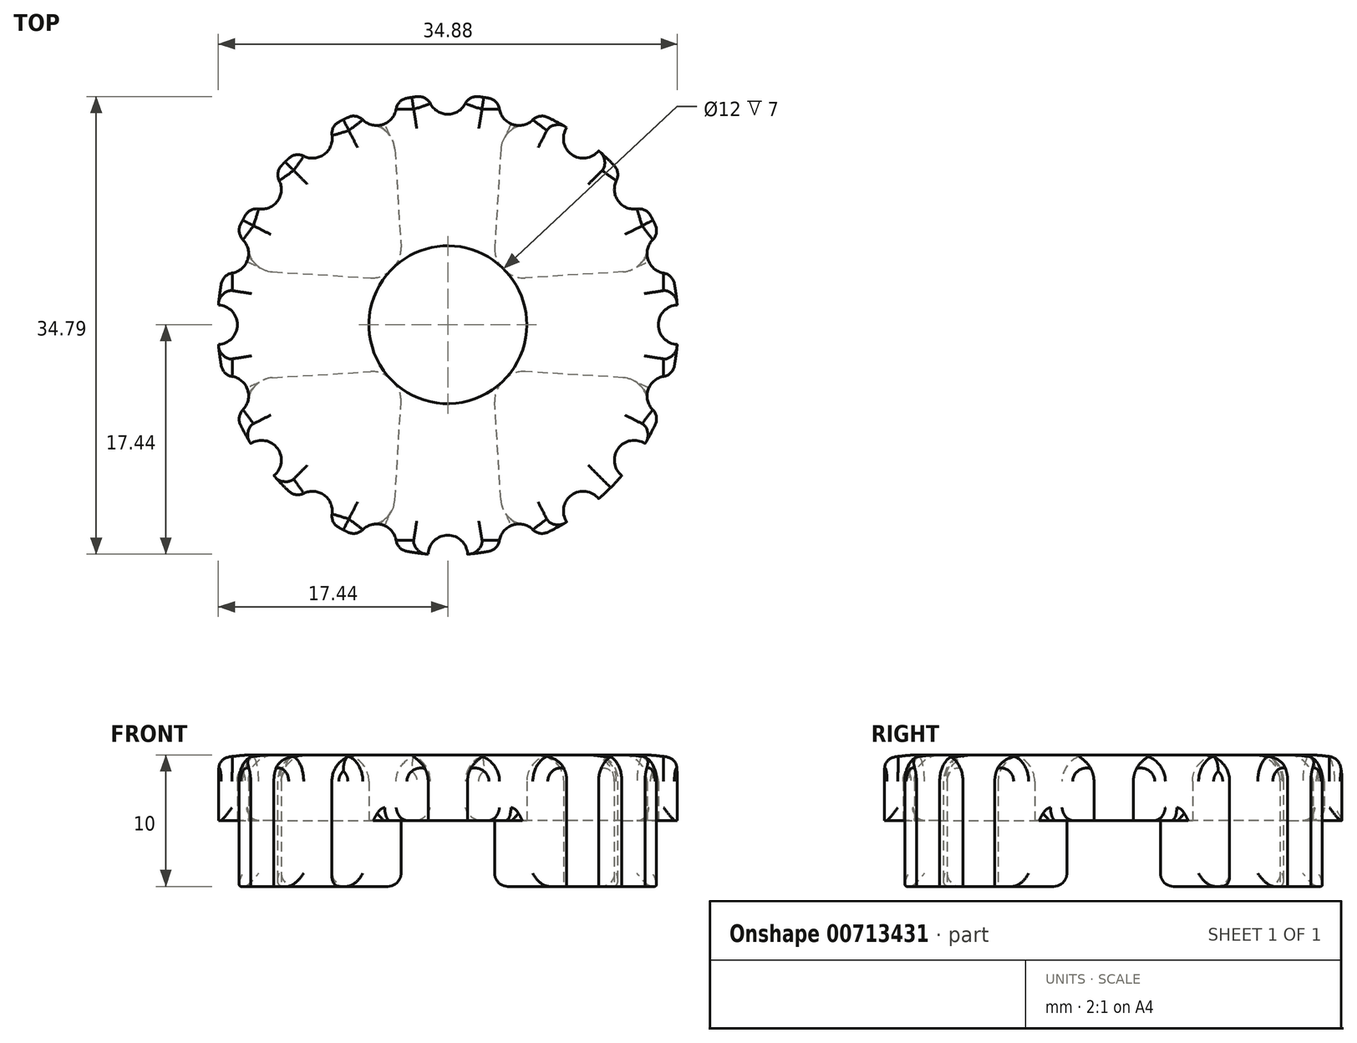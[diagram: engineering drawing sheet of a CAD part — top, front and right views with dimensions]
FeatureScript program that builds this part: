
annotation { "Feature Type Name" : "Feature", "Feature Type Description" : "" }
export const myFeature = defineFeature(function(context is Context, id is Id, definition is map)
    precondition{}
    {
        {
            var Q0;
            Q0=qCreatedBy(makeId("Top.planeOp"),FACE);
            var sketch = newSketch(context, id + "F0", { "sketchPlane" : qUnion([Q0])});
            skCircle(sketch, "E0", {"center": v(0, 0) * mm, "radius": 17.5 * mm});
            skCircle(sketch, "E1", {"center": v(0, 0) * mm, "radius": 6 * mm});
            skPoint(sketch, "E2", {"position": v(-3.5, 4.87) * mm});
            skPoint(sketch, "E3.MirrorP", {"position": v(3.5, 4.87) * mm});
            skPoint(sketch, "E4", {"position": v(-4.25, 16.98) * mm});
            skPoint(sketch, "E5.MirrorP", {"position": v(4.25, 16.98) * mm});
            skLineSegment(sketch, "E6", {"start": v(-4.25, 16.98) * mm, "end": v(-3.5, 4.87) * mm});
            skLineSegment(sketch, "E7", {"start": v(4.25, 16.98) * mm, "end": v(3.5, 4.87) * mm});
            skLineSegment(sketch, "E8.1.0", {"start": v(-16.98, 4.25) * mm, "end": v(-4.87, 3.5) * mm});
            skLineSegment(sketch, "E8.1.1", {"start": v(-16.98, -4.25) * mm, "end": v(-4.87, -3.5) * mm});
            skLineSegment(sketch, "E8.2.0", {"start": v(-4.25, -16.98) * mm, "end": v(-3.5, -4.87) * mm});
            skLineSegment(sketch, "E8.2.1", {"start": v(4.25, -16.98) * mm, "end": v(3.5, -4.87) * mm});
            skLineSegment(sketch, "E8.3.0", {"start": v(16.98, -4.25) * mm, "end": v(4.87, -3.5) * mm});
            skLineSegment(sketch, "E8.3.1", {"start": v(16.98, 4.25) * mm, "end": v(4.87, 3.5) * mm});
            skCircle(sketch, "E9", {"center": v(0, 17.5) * mm, "radius": 1.5 * mm});
            skCircle(sketch, "E10.1.0", {"center": v(-5.4, 16.64) * mm, "radius": 1.5 * mm});
            skCircle(sketch, "E10.2.0", {"center": v(-10.29, 14.16) * mm, "radius": 1.5 * mm});
            skCircle(sketch, "E11.1.3.0", {"center": v(-14.16, 10.29) * mm, "radius": 1.5 * mm});
            skCircle(sketch, "E11.1.4.0", {"center": v(-16.64, 5.4) * mm, "radius": 1.5 * mm});
            skCircle(sketch, "E11.1.5.0", {"center": v(-17.5, 0) * mm, "radius": 1.5 * mm});
            skCircle(sketch, "E11.1.6.0", {"center": v(-16.64, -5.4) * mm, "radius": 1.5 * mm});
            skCircle(sketch, "E11.1.7.0", {"center": v(-14.16, -10.29) * mm, "radius": 1.5 * mm});
            skCircle(sketch, "E11.1.8.0", {"center": v(-10.29, -14.16) * mm, "radius": 1.5 * mm});
            skCircle(sketch, "E11.1.9.0", {"center": v(-5.4, -16.64) * mm, "radius": 1.5 * mm});
            skCircle(sketch, "E11.1.10.0", {"center": v(0, -17.5) * mm, "radius": 1.5 * mm});
            skCircle(sketch, "E11.1.11.0", {"center": v(5.4, -16.64) * mm, "radius": 1.5 * mm});
            skCircle(sketch, "E11.1.12.0", {"center": v(10.29, -14.16) * mm, "radius": 1.5 * mm});
            skCircle(sketch, "E11.1.13.0", {"center": v(14.16, -10.29) * mm, "radius": 1.5 * mm});
            skCircle(sketch, "E11.1.14.0", {"center": v(16.64, -5.4) * mm, "radius": 1.5 * mm});
            skCircle(sketch, "E11.1.15.0", {"center": v(17.5, 0) * mm, "radius": 1.5 * mm});
            skCircle(sketch, "E11.1.16.0", {"center": v(16.64, 5.4) * mm, "radius": 1.5 * mm});
            skCircle(sketch, "E11.1.17.0", {"center": v(14.16, 10.29) * mm, "radius": 1.5 * mm});
            skCircle(sketch, "E11.1.18.0", {"center": v(10.29, 14.16) * mm, "radius": 1.5 * mm});
            skCircle(sketch, "E11.1.19.0", {"center": v(5.4, 16.64) * mm, "radius": 1.5 * mm});
            skSolve(sketch);
        }
        {
            var Q0;
            {var subQ0=sQuery(id+"F0.wireOp",EDGE,"E11.1.6.0");var subQ6=sQuery(id+"F0.wireOp",EDGE,"E0");var subQ14=makeQuery(id+"F0.imprint","INTERSECT",VERTEX,{"disambiguationData":[OD(1.0)],"derivedFrom":[subQ6,subQ0]});Q0=makeQuery(id+"F0.imprint","IMPRINT",FACE,{"disambiguationData":[TD([[makeQuery(id+"F0.imprint","IMPRINT",EDGE,{"disambiguationData":[TD([[subQ14,-1.0]])],"derivedFrom":subQ6}),1.0]])]});}
            var Q1;
            {var subQ0=sQuery(id+"F0.wireOp",EDGE,"E11.1.11.0");var subQ5=sQuery(id+"F0.wireOp",EDGE,"E0");var subQ6=makeQuery(id+"F0.imprint","INTERSECT",VERTEX,{"disambiguationData":[OD(1.0)],"derivedFrom":[subQ5,subQ0]});Q1=makeQuery(id+"F0.imprint","IMPRINT",FACE,{"disambiguationData":[TD([[makeQuery(id+"F0.imprint","IMPRINT",EDGE,{"disambiguationData":[TD([[subQ6,-1.0]])],"derivedFrom":subQ5}),1.0]])]});}
            var Q2;
            {var subQ1=sQuery(id+"F0.wireOp",EDGE,"E0");var subQ12=sQuery(id+"F0.wireOp",EDGE,"E11.1.16.0");var subQ13=makeQuery(id+"F0.imprint","INTERSECT",VERTEX,{"disambiguationData":[OD(1.0)],"derivedFrom":[subQ1,subQ12]});Q2=makeQuery(id+"F0.imprint","IMPRINT",FACE,{"disambiguationData":[TD([[makeQuery(id+"F0.imprint","IMPRINT",EDGE,{"disambiguationData":[TD([[subQ13,-1.0]])],"derivedFrom":subQ1}),1.0]])]});}
            var Q3;
            {var subQ1=sQuery(id+"F0.wireOp",EDGE,"E0");var subQ12=sQuery(id+"F0.wireOp",EDGE,"E10.1.0");var subQ15=makeQuery(id+"F0.imprint","INTERSECT",VERTEX,{"disambiguationData":[OD(1.0)],"derivedFrom":[subQ1,subQ12]});Q3=makeQuery(id+"F0.imprint","IMPRINT",FACE,{"disambiguationData":[TD([[makeQuery(id+"F0.imprint","IMPRINT",EDGE,{"disambiguationData":[TD([[subQ15,-1.0]])],"derivedFrom":subQ1}),1.0]])]});}
            extrude(context, id + "F1", {"entities" : qUnion([Q0, Q1, Q2, Q3]), "depth" : 10 * mm, "offsetDistance" : 25 * mm});
        }
        {
            var Q0;
            {var subQ5=sQuery(id+"F0.wireOp",EDGE,"E11.1.9.0");var subQ6=sQuery(id+"F0.wireOp",EDGE,"E0");var subQ7=makeQuery(id+"F0.imprint","INTERSECT",VERTEX,{"disambiguationData":[OD(1.0)],"derivedFrom":[subQ6,subQ5]});Q0=makeQuery(id+"F0.imprint","IMPRINT",FACE,{"disambiguationData":[TD([[makeQuery(id+"F0.imprint","IMPRINT",EDGE,{"disambiguationData":[TD([[subQ7,-1.0]])],"derivedFrom":subQ6}),1.0]])]});}
            var Q1;
            {var subQ8=sQuery(id+"F0.wireOp",EDGE,"E0");var subQ14=sQuery(id+"F0.wireOp",EDGE,"E11.1.4.0");var subQ15=makeQuery(id+"F0.imprint","INTERSECT",VERTEX,{"disambiguationData":[OD(1.0)],"derivedFrom":[subQ8,subQ14]});Q1=makeQuery(id+"F0.imprint","IMPRINT",FACE,{"disambiguationData":[TD([[makeQuery(id+"F0.imprint","IMPRINT",EDGE,{"disambiguationData":[TD([[subQ15,-1.0]])],"derivedFrom":subQ8}),1.0]])]});}
            var Q2;
            {var subQ6=sQuery(id+"F0.wireOp",EDGE,"E0");var subQ13=sQuery(id+"F0.wireOp",EDGE,"E11.1.16.0");var subQ14=makeQuery(id+"F0.imprint","INTERSECT",VERTEX,{"disambiguationData":[OD(0.0)],"derivedFrom":[subQ6,subQ13]});Q2=makeQuery(id+"F0.imprint","IMPRINT",FACE,{"disambiguationData":[TD([[makeQuery(id+"F0.imprint","IMPRINT",EDGE,{"disambiguationData":[TD([[subQ14,1.0]])],"derivedFrom":subQ6}),1.0]])]});}
            var Q3;
            {var subQ5=sQuery(id+"F0.wireOp",EDGE,"E11.1.19.0");var subQ14=sQuery(id+"F0.wireOp",EDGE,"E0");var subQ17=makeQuery(id+"F0.imprint","INTERSECT",VERTEX,{"disambiguationData":[OD(1.0)],"derivedFrom":[subQ14,subQ5]});Q3=makeQuery(id+"F0.imprint","IMPRINT",FACE,{"disambiguationData":[TD([[makeQuery(id+"F0.imprint","IMPRINT",EDGE,{"disambiguationData":[TD([[subQ17,-1.0]])],"derivedFrom":subQ14}),1.0]])]});}
            var Q4;
            {var subQ0=sQuery(id+"F0.wireOp",EDGE,"E6");var subQ1=sQuery(id+"F0.wireOp",EDGE,"E1");var subQ2=makeQuery(id+"F0.imprint","INTERSECT",VERTEX,{"derivedFrom":[subQ1,subQ0]});Q4=makeQuery(id+"F0.imprint","IMPRINT",FACE,{"disambiguationData":[TD([[makeQuery(id+"F0.imprint","IMPRINT",EDGE,{"disambiguationData":[TD([[subQ2,1.0]])],"derivedFrom":subQ1}),-1.0]])]});}
            var Q5;
            {var subQ0=sQuery(id+"F0.wireOp",EDGE,"E7");var subQ1=sQuery(id+"F0.wireOp",EDGE,"E1");var subQ2=makeQuery(id+"F0.imprint","INTERSECT",VERTEX,{"derivedFrom":[subQ1,subQ0]});Q5=makeQuery(id+"F0.imprint","IMPRINT",FACE,{"disambiguationData":[TD([[makeQuery(id+"F0.imprint","IMPRINT",EDGE,{"disambiguationData":[TD([[subQ2,-1.0]])],"derivedFrom":subQ1}),-1.0]])]});}
            var Q6;
            {var subQ0=sQuery(id+"F0.wireOp",EDGE,"E8.2.1");var subQ1=sQuery(id+"F0.wireOp",EDGE,"E1");var subQ2=makeQuery(id+"F0.imprint","INTERSECT",VERTEX,{"derivedFrom":[subQ1,subQ0]});Q6=makeQuery(id+"F0.imprint","IMPRINT",FACE,{"disambiguationData":[TD([[makeQuery(id+"F0.imprint","IMPRINT",EDGE,{"disambiguationData":[TD([[subQ2,1.0]])],"derivedFrom":subQ1}),-1.0]])]});}
            var Q7;
            {var subQ0=sQuery(id+"F0.wireOp",EDGE,"E8.1.1");var subQ1=sQuery(id+"F0.wireOp",EDGE,"E1");var subQ2=makeQuery(id+"F0.imprint","INTERSECT",VERTEX,{"derivedFrom":[subQ1,subQ0]});Q7=makeQuery(id+"F0.imprint","IMPRINT",FACE,{"disambiguationData":[TD([[makeQuery(id+"F0.imprint","IMPRINT",EDGE,{"disambiguationData":[TD([[subQ2,1.0]])],"derivedFrom":subQ1}),-1.0]])]});}
            extrude(context, id + "F2", {"entities" : qUnion([Q0, Q1, Q2, Q3, Q4, Q5, Q6, Q7]), "operationType" : NewBodyOperationType.ADD, "depth" : 10 * mm, "offsetDistance" : 25 * mm, "hasSecondDirection" : true, "secondDirectionOppositeDirection" : false, "secondDirectionDepth" : 5 * mm});
        }
        {
            var Q0;
            {var subQ0=sQuery(id+"F0.wireOp",EDGE,"E11.1.24.0");var subQ1=sQuery(id+"F0.wireOp",EDGE,"E11.1.20.0");var subQ2=sQuery(id+"F0.wireOp",EDGE,"E11.1.14.0");var subQ3=sQuery(id+"F0.wireOp",EDGE,"E11.1.11.0");var subQ4=sQuery(id+"F0.wireOp",EDGE,"E11.1.5.0");var subQ5=sQuery(id+"F0.wireOp",EDGE,"E10.1.0");var subQ6=sQuery(id+"F0.wireOp",EDGE,"E8.3.1");var subQ7=sQuery(id+"F0.wireOp",EDGE,"E8.3.0");var subQ8=sQuery(id+"F0.wireOp",EDGE,"E8.2.1");var subQ9=sQuery(id+"F0.wireOp",EDGE,"E8.2.0");var subQ10=sQuery(id+"F0.wireOp",EDGE,"E8.1.1");var subQ11=sQuery(id+"F0.wireOp",EDGE,"E8.1.0");var subQ12=sQuery(id+"F0.wireOp",EDGE,"E7");var subQ13=sQuery(id+"F0.wireOp",EDGE,"E6");var subQ14=sQuery(id+"F0.wireOp",EDGE,"E0");Q0=makeQuery(id+"F2.boolean.opBoolean","MERGE",FACE,{"derivedFrom":[makeQuery(id+"F1.opExtrude","CAP_FACE",FACE,{"disambiguationData":[OSD([subQ14,subQ12,subQ6,subQ1,sQuery(id+"F0.wireOp",EDGE,"E11.1.21.0"),sQuery(id+"F0.wireOp",EDGE,"E11.1.22.0"),sQuery(id+"F0.wireOp",EDGE,"E11.1.23.0"),subQ0])],"isStart":false}),makeQuery(id+"F1.opExtrude","CAP_FACE",FACE,{"disambiguationData":[OSD([subQ14,subQ13,subQ11,subQ5,sQuery(id+"F0.wireOp",EDGE,"E10.2.0"),sQuery(id+"F0.wireOp",EDGE,"E11.1.3.0"),sQuery(id+"F0.wireOp",EDGE,"E11.1.4.0"),subQ4])],"isStart":false}),makeQuery(id+"F1.opExtrude","CAP_FACE",FACE,{"disambiguationData":[OSD([subQ14,subQ10,subQ9,sQuery(id+"F0.wireOp",EDGE,"E11.1.8.0"),sQuery(id+"F0.wireOp",EDGE,"E11.1.9.0"),sQuery(id+"F0.wireOp",EDGE,"E11.1.10.0"),subQ3])],"isStart":false}),makeQuery(id+"F1.opExtrude","CAP_FACE",FACE,{"disambiguationData":[OSD([subQ14,subQ8,subQ7,subQ2,sQuery(id+"F0.wireOp",EDGE,"E11.1.15.0"),sQuery(id+"F0.wireOp",EDGE,"E11.1.16.0"),sQuery(id+"F0.wireOp",EDGE,"E11.1.17.0")])],"isStart":false}),makeQuery(id+"F2.opExtrude","CAP_FACE",FACE,{"disambiguationData":[OSD([subQ14,sQuery(id+"F0.wireOp",EDGE,"E1"),subQ13,subQ12,subQ11,subQ10,subQ9,subQ8,subQ7,subQ6,sQuery(id+"F0.wireOp",EDGE,"E9"),subQ5,subQ4,sQuery(id+"F0.wireOp",EDGE,"E11.1.6.0"),sQuery(id+"F0.wireOp",EDGE,"E11.1.7.0"),subQ3,sQuery(id+"F0.wireOp",EDGE,"E11.1.12.0"),sQuery(id+"F0.wireOp",EDGE,"E11.1.13.0"),subQ2,sQuery(id+"F0.wireOp",EDGE,"E11.1.18.0"),sQuery(id+"F0.wireOp",EDGE,"E11.1.19.0"),subQ1,subQ0])],"isStart":false})]});}
            var Q1;
            Q1=makeQuery(id+"F1.opExtrude","SWEPT_EDGE",EDGE,{"disambiguationData":[OSD([sQuery(id+"F0.wireOp",EDGE,"E6"),sQuery(id+"F0.wireOp",EDGE,"E8.1.0")])]});
            var Q2;
            Q2=makeQuery(id+"F1.opExtrude","SWEPT_EDGE",EDGE,{"disambiguationData":[OSD([sQuery(id+"F0.wireOp",EDGE,"E8.1.1"),sQuery(id+"F0.wireOp",EDGE,"E8.2.0")])]});
            var Q3;
            Q3=makeQuery(id+"F1.opExtrude","SWEPT_EDGE",EDGE,{"disambiguationData":[OSD([sQuery(id+"F0.wireOp",EDGE,"E8.2.1"),sQuery(id+"F0.wireOp",EDGE,"E8.3.0")])]});
            var Q4;
            Q4=makeQuery(id+"F1.opExtrude","SWEPT_EDGE",EDGE,{"disambiguationData":[OSD([sQuery(id+"F0.wireOp",EDGE,"E7"),sQuery(id+"F0.wireOp",EDGE,"E8.3.1")])]});
            fillet(context, id + "F3", {"entities" : qUnion([Q0, Q1, Q2, Q3, Q4]), "radius" : 2 * mm, "tangentPropagation" : true, "allowEdgeOverflow" : false});
        }
        {
            var Q0;
            Q0=makeQuery(id+"F1.opExtrude","SWEPT_FACE",FACE,{"disambiguationData":[OSD([sQuery(id+"F0.wireOp",EDGE,"E11.1.8.0")])]});
            var Q1;
            Q1=makeQuery(id+"F1.opExtrude","SWEPT_FACE",FACE,{"disambiguationData":[OSD([sQuery(id+"F0.wireOp",EDGE,"E11.1.9.0")])]});
            var Q2;
            Q2=makeQuery(id+"F1.opExtrude","SWEPT_FACE",FACE,{"disambiguationData":[OSD([sQuery(id+"F0.wireOp",EDGE,"E11.1.10.0")])]});
            var Q3;
            {var subQ0=sQuery(id+"F0.wireOp",EDGE,"E11.1.11.0");Q3=makeQuery(id+"F3.opFillet","BLEND_EDGE",EDGE,{"blendedFrom":[makeQuery(id+"F1.opExtrude","CAP_EDGE",EDGE,{"disambiguationData":[OSD([sQuery(id+"F0.wireOp",EDGE,"E11.1.10.0")])],"isStart":false}),makeQuery(id+"F2.boolean.opBoolean","MERGE",EDGE,{"derivedFrom":[makeQuery(id+"F1.opExtrude","CAP_EDGE",EDGE,{"disambiguationData":[OSD([subQ0])],"isStart":false}),makeQuery(id+"F2.opExtrude","CAP_EDGE",EDGE,{"disambiguationData":[OSD([subQ0])],"isStart":false})]})],"blendedInto":[]});}
            var Q4;
            {var subQ0=sQuery(id+"F0.wireOp",EDGE,"E11.1.11.0");Q4=makeQuery(id+"F2.boolean.opBoolean","MERGE",FACE,{"derivedFrom":[makeQuery(id+"F1.opExtrude","SWEPT_FACE",FACE,{"disambiguationData":[OSD([subQ0])]}),makeQuery(id+"F2.opExtrude","SWEPT_FACE",FACE,{"disambiguationData":[OSD([subQ0])]})]});}
            var Q5;
            Q5=makeQuery(id+"F2.opExtrude","SWEPT_FACE",FACE,{"disambiguationData":[OSD([sQuery(id+"F0.wireOp",EDGE,"E11.1.12.0")])]});
            var Q6;
            Q6=makeQuery(id+"F2.opExtrude","SWEPT_FACE",FACE,{"disambiguationData":[OSD([sQuery(id+"F0.wireOp",EDGE,"E11.1.13.0")])]});
            var Q7;
            {var subQ0=sQuery(id+"F0.wireOp",EDGE,"E11.1.14.0");Q7=makeQuery(id+"F2.boolean.opBoolean","MERGE",FACE,{"derivedFrom":[makeQuery(id+"F1.opExtrude","SWEPT_FACE",FACE,{"disambiguationData":[OSD([subQ0])]}),makeQuery(id+"F2.opExtrude","SWEPT_FACE",FACE,{"disambiguationData":[OSD([subQ0])]})]});}
            var Q8;
            Q8=makeQuery(id+"F1.opExtrude","SWEPT_FACE",FACE,{"disambiguationData":[OSD([sQuery(id+"F0.wireOp",EDGE,"E11.1.15.0")])]});
            var Q9;
            Q9=makeQuery(id+"F1.opExtrude","SWEPT_FACE",FACE,{"disambiguationData":[OSD([sQuery(id+"F0.wireOp",EDGE,"E11.1.16.0")])]});
            var Q10;
            Q10=makeQuery(id+"F1.opExtrude","SWEPT_FACE",FACE,{"disambiguationData":[OSD([sQuery(id+"F0.wireOp",EDGE,"E11.1.17.0")])]});
            var Q11;
            Q11=makeQuery(id+"F2.opExtrude","SWEPT_FACE",FACE,{"disambiguationData":[OSD([sQuery(id+"F0.wireOp",EDGE,"E11.1.18.0")])]});
            var Q12;
            Q12=makeQuery(id+"F2.opExtrude","SWEPT_FACE",FACE,{"disambiguationData":[OSD([sQuery(id+"F0.wireOp",EDGE,"E11.1.19.0")])]});
            var Q13;
            {var subQ0=sQuery(id+"F0.wireOp",EDGE,"E11.1.20.0");Q13=makeQuery(id+"F2.boolean.opBoolean","MERGE",FACE,{"derivedFrom":[makeQuery(id+"F1.opExtrude","SWEPT_FACE",FACE,{"disambiguationData":[OSD([subQ0])]}),makeQuery(id+"F2.opExtrude","SWEPT_FACE",FACE,{"disambiguationData":[OSD([subQ0])]})]});}
            var Q14;
            Q14=makeQuery(id+"F1.opExtrude","SWEPT_FACE",FACE,{"disambiguationData":[OSD([sQuery(id+"F0.wireOp",EDGE,"E11.1.21.0")])]});
            var Q15;
            Q15=makeQuery(id+"F1.opExtrude","SWEPT_FACE",FACE,{"disambiguationData":[OSD([sQuery(id+"F0.wireOp",EDGE,"E11.1.22.0")])]});
            var Q16;
            Q16=makeQuery(id+"F1.opExtrude","SWEPT_FACE",FACE,{"disambiguationData":[OSD([sQuery(id+"F0.wireOp",EDGE,"E11.1.23.0")])]});
            var Q17;
            {var subQ0=sQuery(id+"F0.wireOp",EDGE,"E11.1.24.0");Q17=makeQuery(id+"F2.boolean.opBoolean","MERGE",FACE,{"derivedFrom":[makeQuery(id+"F1.opExtrude","SWEPT_FACE",FACE,{"disambiguationData":[OSD([subQ0])]}),makeQuery(id+"F2.opExtrude","SWEPT_FACE",FACE,{"disambiguationData":[OSD([subQ0])]})]});}
            var Q18;
            Q18=makeQuery(id+"F2.opExtrude","SWEPT_FACE",FACE,{"disambiguationData":[OSD([sQuery(id+"F0.wireOp",EDGE,"E9")])]});
            var Q19;
            {var subQ0=sQuery(id+"F0.wireOp",EDGE,"E10.1.0");Q19=makeQuery(id+"F2.boolean.opBoolean","MERGE",FACE,{"derivedFrom":[makeQuery(id+"F1.opExtrude","SWEPT_FACE",FACE,{"disambiguationData":[OSD([subQ0])]}),makeQuery(id+"F2.opExtrude","SWEPT_FACE",FACE,{"disambiguationData":[OSD([subQ0])]})]});}
            var Q20;
            Q20=makeQuery(id+"F1.opExtrude","SWEPT_FACE",FACE,{"disambiguationData":[OSD([sQuery(id+"F0.wireOp",EDGE,"E10.2.0")])]});
            var Q21;
            Q21=makeQuery(id+"F1.opExtrude","SWEPT_FACE",FACE,{"disambiguationData":[OSD([sQuery(id+"F0.wireOp",EDGE,"E11.1.3.0")])]});
            var Q22;
            Q22=makeQuery(id+"F1.opExtrude","SWEPT_FACE",FACE,{"disambiguationData":[OSD([sQuery(id+"F0.wireOp",EDGE,"E11.1.4.0")])]});
            var Q23;
            {var subQ0=sQuery(id+"F0.wireOp",EDGE,"E11.1.5.0");Q23=makeQuery(id+"F2.boolean.opBoolean","MERGE",FACE,{"derivedFrom":[makeQuery(id+"F1.opExtrude","SWEPT_FACE",FACE,{"disambiguationData":[OSD([subQ0])]}),makeQuery(id+"F2.opExtrude","SWEPT_FACE",FACE,{"disambiguationData":[OSD([subQ0])]})]});}
            var Q24;
            Q24=makeQuery(id+"F2.opExtrude","SWEPT_FACE",FACE,{"disambiguationData":[OSD([sQuery(id+"F0.wireOp",EDGE,"E11.1.6.0")])]});
            var Q25;
            Q25=makeQuery(id+"F2.opExtrude","SWEPT_FACE",FACE,{"disambiguationData":[OSD([sQuery(id+"F0.wireOp",EDGE,"E11.1.7.0")])]});
            fillet(context, id + "F4", {"entities" : qUnion([Q0, Q1, Q2, Q3, Q4, Q5, Q6, Q7, Q8, Q9, Q10, Q11, Q12, Q13, Q14, Q15, Q16, Q17, Q18, Q19, Q20, Q21, Q22, Q23, Q24, Q25]), "radius" : 1 * mm, "tangentPropagation" : true, "allowEdgeOverflow" : false});
        }
    });
